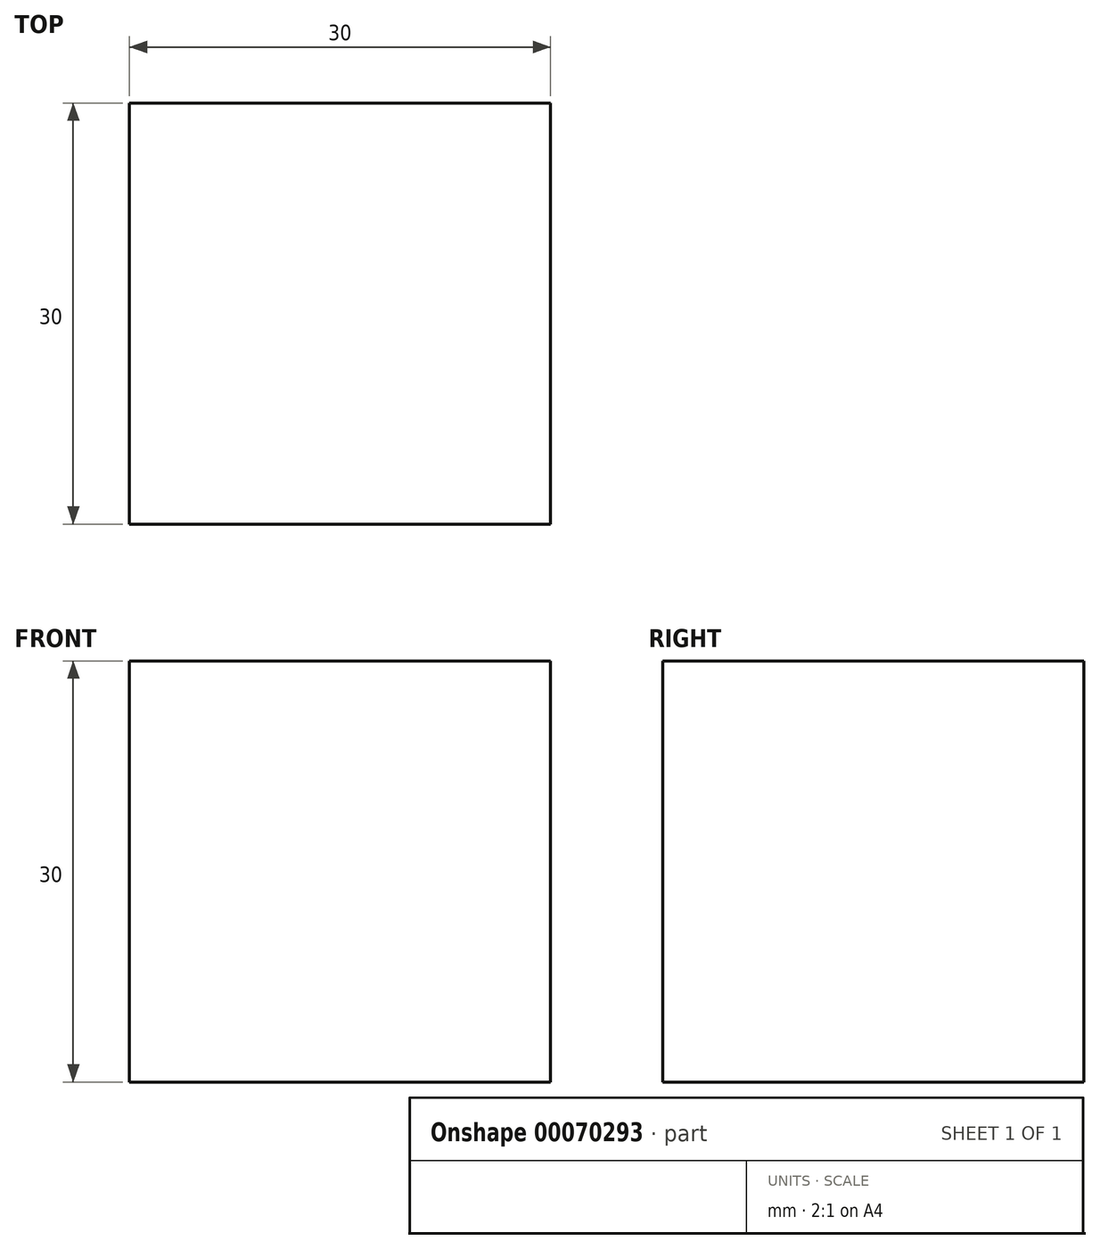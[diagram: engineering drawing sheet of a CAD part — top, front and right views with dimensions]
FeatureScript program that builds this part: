
annotation { "Feature Type Name" : "Feature", "Feature Type Description" : "" }
export const myFeature = defineFeature(function(context is Context, id is Id, definition is map)
    precondition{}
    {
        {
            var Q0;
            Q0=qCreatedBy(makeId("Top.planeOp"),FACE);
            var sketch = newSketch(context, id + "F0", { "sketchPlane" : qUnion([Q0])});
            skLineSegment(sketch, "E0.bottom", {"start": v(-52.1, 49.65) * mm, "end": v(-22.1, 49.65) * mm});
            skLineSegment(sketch, "E0.top", {"start": v(-52.1, 19.65) * mm, "end": v(-22.1, 19.65) * mm});
            skLineSegment(sketch, "E0.left", {"start": v(-52.1, 49.65) * mm, "end": v(-52.1, 19.65) * mm});
            skLineSegment(sketch, "E0.right", {"start": v(-22.1, 49.65) * mm, "end": v(-22.1, 19.65) * mm});
            skSolve(sketch);
        }
        {
            var Q0;
            Q0=makeQuery(id+"F0.imprint","IMPRINT",FACE,{"disambiguationData":[TD([[makeQuery(id+"F0.imprint","IMPRINT",EDGE,{"derivedFrom":sQuery(id+"F0.wireOp",EDGE,"E0.bottom")}),-1.0]])]});
            extrude(context, id + "F1", {"entities" : qUnion([Q0]), "depth" : 30 * mm});
        }
    });
